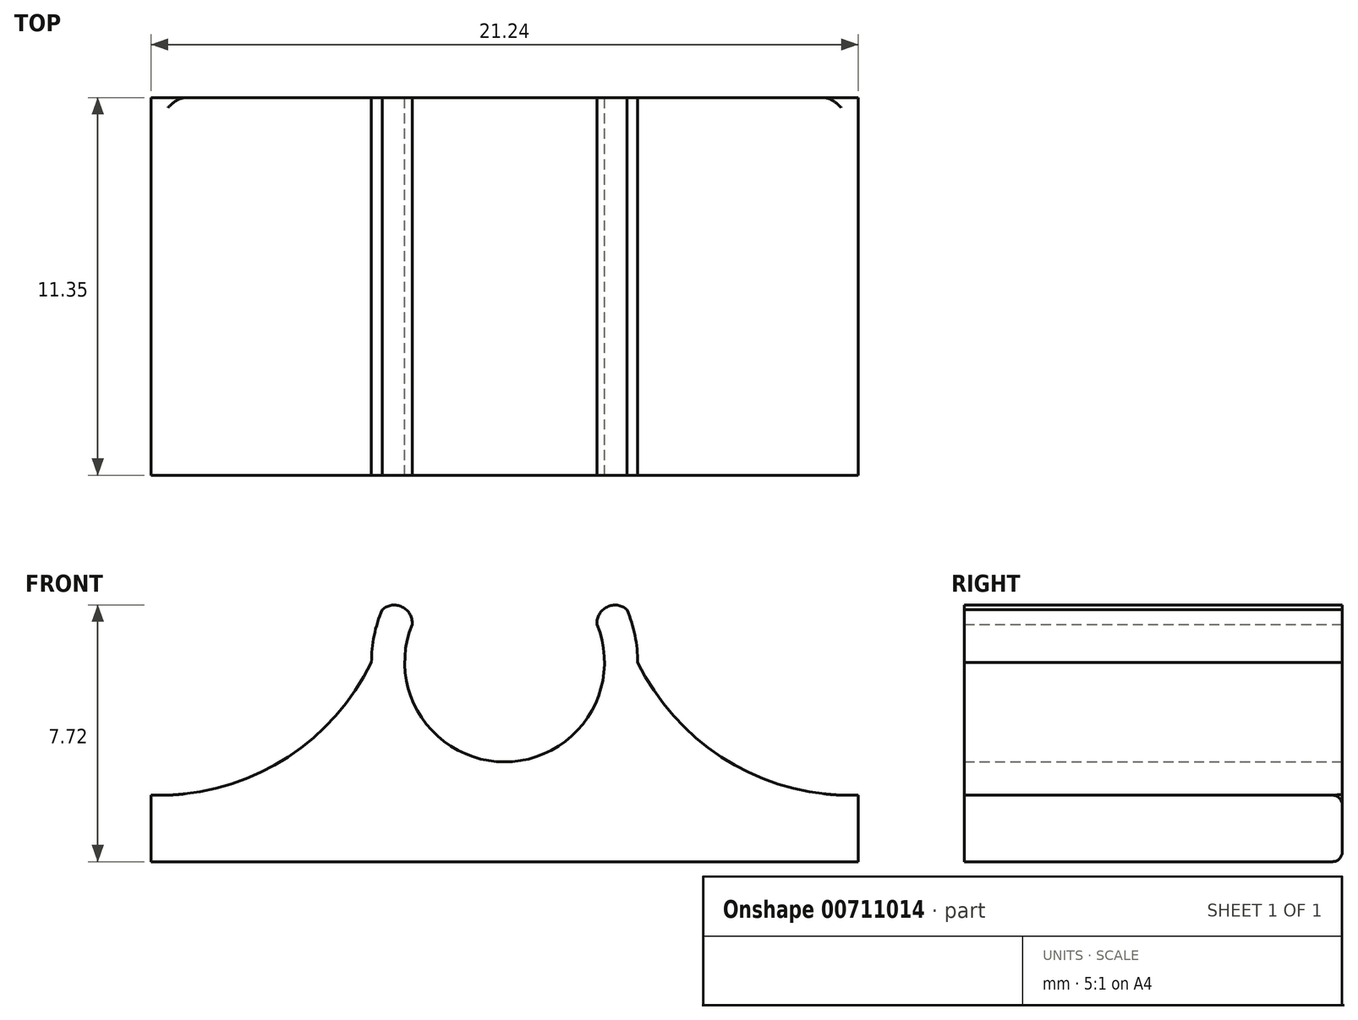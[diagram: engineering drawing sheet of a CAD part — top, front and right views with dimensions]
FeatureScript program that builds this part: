
annotation { "Feature Type Name" : "Feature", "Feature Type Description" : "" }
export const myFeature = defineFeature(function(context is Context, id is Id, definition is map)
    precondition{}
    {
        {
            var Q0;
            Q0=qCreatedBy(makeId("Top.planeOp"),FACE);
            var sketch = newSketch(context, id + "F0", { "sketchPlane" : qUnion([Q0])});
            skLineSegment(sketch, "E0.bottom", {"start": v(-45, 20) * mm, "end": v(45, 20) * mm});
            skLineSegment(sketch, "E0.top", {"start": v(-45, -20) * mm, "end": v(45, -20) * mm});
            skLineSegment(sketch, "E0.left", {"start": v(-55, 10) * mm, "end": v(-55, -10) * mm});
            skLineSegment(sketch, "E0.right", {"start": v(55, 10) * mm, "end": v(55, -10) * mm});
            skPoint(sketch, "E1.visualSharp", {"position": v(-55, 20) * mm});
            skArc(sketch, "E1.filletArc", {"start": v(-45, 20) * mm, "mid": v(-52.07, 17.07) * mm, "end": v(-55, 10) * mm});
            skPoint(sketch, "E2.visualSharp", {"position": v(55, 20) * mm});
            skArc(sketch, "E2.filletArc", {"start": v(55, 10) * mm, "mid": v(52.07, 17.07) * mm, "end": v(45, 20) * mm});
            skPoint(sketch, "E3.visualSharp", {"position": v(55, -20) * mm});
            skArc(sketch, "E3.filletArc", {"start": v(45, -20) * mm, "mid": v(52.07, -17.07) * mm, "end": v(55, -10) * mm});
            skPoint(sketch, "E4.visualSharp", {"position": v(-55, -20) * mm});
            skArc(sketch, "E4.filletArc", {"start": v(-55, -10) * mm, "mid": v(-52.07, -17.07) * mm, "end": v(-45, -20) * mm});
            skSolve(sketch);
        }
        {
            var Q0;
            Q0=qSketchRegion(id+"F0",true);
            extrude(context, id + "F1", {"entities" : qUnion([Q0]), "depth" : 2 * mm, "offsetDistance" : 25 * mm});
        }
        {
            var Q0;
            Q0=makeQuery(id+"F1.opExtrude","SWEPT_FACE",FACE,{"disambiguationData":[OSD([sQuery(id+"F0.wireOp",EDGE,"E0.bottom")])]});
            var sketch = newSketch(context, id + "F2", { "sketchPlane" : qUnion([Q0])});
            skArc(sketch, "E5", {"start": v(-2.78, 7.13) * mm, "mid": v(0, 3) * mm, "end": v(2.78, 7.13) * mm});
            skArc(sketch, "E6", {"start": v(-3.67, 7.58) * mm, "mid": v(-3.92, 6.8) * mm, "end": v(-4, 6) * mm});
            skArc(sketch, "E7", {"start": v(4, 6) * mm, "mid": v(6.5, 3.15) * mm, "end": v(10.12, 2) * mm});
            skArc(sketch, "E8.MirrorCS", {"start": v(-4, 6) * mm, "mid": v(-6.5, 3.15) * mm, "end": v(-10.12, 2) * mm});
            skArc(sketch, "E9", {"start": v(3.67, 7.58) * mm, "mid": v(3.08, 7.66) * mm, "end": v(2.78, 7.13) * mm});
            skArc(sketch, "E10.MirrorCS", {"start": v(-3.67, 7.58) * mm, "mid": v(-3.08, 7.66) * mm, "end": v(-2.78, 7.13) * mm});
            skArc(sketch, "E11.trimOffspring", {"start": v(4, 6) * mm, "mid": v(3.92, 6.8) * mm, "end": v(3.67, 7.58) * mm});
            skLineSegment(sketch, "E12", {"start": v(-10.12, 2) * mm, "end": v(10.12, 2) * mm});
            skSolve(sketch);
        }
        {
            var Q0;
            Q0=qSketchRegion(id+"F2",true);
            var Q1;
            Q1=makeQuery(id+"F1.opExtrude","SWEPT_FACE",FACE,{"disambiguationData":[OSD([sQuery(id+"F0.wireOp",EDGE,"E0.top")])]});
            extrude(context, id + "F3", {"entities" : qUnion([Q0]), "operationType" : NewBodyOperationType.ADD, "endBound" : BoundingType.UP_TO_SURFACE, "oppositeDirection" : true, "depth" : 25 * mm, "endBoundEntityFace" : qUnion([Q1]), "offsetDistance" : 25 * mm});
        }
        {
            var Q0;
            Q0=makeQuery(id+"F1.opExtrude","CAP_FACE",FACE,{"disambiguationData":[OSD([sQuery(id+"F0.wireOp",EDGE,"E0.bottom"),sQuery(id+"F0.wireOp",EDGE,"E0.top"),sQuery(id+"F0.wireOp",EDGE,"E0.left"),sQuery(id+"F0.wireOp",EDGE,"E0.right"),sQuery(id+"F0.wireOp",EDGE,"E1.filletArc"),sQuery(id+"F0.wireOp",EDGE,"E2.filletArc"),sQuery(id+"F0.wireOp",EDGE,"E3.filletArc"),sQuery(id+"F0.wireOp",EDGE,"E4.filletArc")])],"isStart":true});
            var Q1;
            {var subQ0=sQuery(id+"F0.wireOp",EDGE,"E2.filletArc");var subQ1=sQuery(id+"F0.wireOp",EDGE,"E0.top");var subQ3=sQuery(id+"F0.wireOp",EDGE,"E0.right");var subQ4=sQuery(id+"F0.wireOp",EDGE,"E0.bottom");var subQ5=sQuery(id+"F0.wireOp",EDGE,"E3.filletArc");Q1=makeQuery(id+"F3.boolean.opBoolean","SPLIT",FACE,{"disambiguationData":[TD([makeQuery(id+"F1.opExtrude","SWEPT_FACE",FACE,{"disambiguationData":[OSD([subQ3])]})])],"derivedFrom":makeQuery(id+"F1.opExtrude","CAP_FACE",FACE,{"disambiguationData":[OSD([subQ4,subQ1,sQuery(id+"F0.wireOp",EDGE,"E0.left"),subQ3,sQuery(id+"F0.wireOp",EDGE,"E1.filletArc"),subQ0,subQ5,sQuery(id+"F0.wireOp",EDGE,"E4.filletArc")])],"isStart":false})});}
            var Q2;
            {var subQ0=sQuery(id+"F0.wireOp",EDGE,"E1.filletArc");var subQ1=sQuery(id+"F0.wireOp",EDGE,"E0.left");var subQ2=sQuery(id+"F0.wireOp",EDGE,"E0.top");var subQ4=sQuery(id+"F0.wireOp",EDGE,"E0.bottom");var subQ5=sQuery(id+"F0.wireOp",EDGE,"E4.filletArc");Q2=makeQuery(id+"F3.boolean.opBoolean","SPLIT",FACE,{"disambiguationData":[TD([makeQuery(id+"F1.opExtrude","SWEPT_FACE",FACE,{"disambiguationData":[OSD([subQ1])]})])],"derivedFrom":makeQuery(id+"F1.opExtrude","CAP_FACE",FACE,{"disambiguationData":[OSD([subQ4,subQ2,subQ1,sQuery(id+"F0.wireOp",EDGE,"E0.right"),subQ0,sQuery(id+"F0.wireOp",EDGE,"E2.filletArc"),sQuery(id+"F0.wireOp",EDGE,"E3.filletArc"),subQ5])],"isStart":false})});}
            fillet(context, id + "F4", {"entities" : qUnion([Q0, Q1, Q2]), "radius" : .3 * mm, "tangentPropagation" : true, "allowEdgeOverflow" : false});
        }
        {
            var Q0;
            {var subQ0=sQuery(id+"F0.wireOp",EDGE,"E1.filletArc");var subQ1=sQuery(id+"F0.wireOp",EDGE,"E0.left");var subQ2=sQuery(id+"F0.wireOp",EDGE,"E0.top");var subQ4=sQuery(id+"F0.wireOp",EDGE,"E0.bottom");var subQ5=sQuery(id+"F0.wireOp",EDGE,"E4.filletArc");Q0=makeQuery(id+"F3.boolean.opBoolean","SPLIT",FACE,{"disambiguationData":[TD([makeQuery(id+"F1.opExtrude","SWEPT_FACE",FACE,{"disambiguationData":[OSD([subQ1])]})])],"derivedFrom":makeQuery(id+"F1.opExtrude","CAP_FACE",FACE,{"disambiguationData":[OSD([subQ4,subQ2,subQ1,sQuery(id+"F0.wireOp",EDGE,"E0.right"),subQ0,sQuery(id+"F0.wireOp",EDGE,"E2.filletArc"),sQuery(id+"F0.wireOp",EDGE,"E3.filletArc"),subQ5])],"isStart":false})});}
            var sketch = newSketch(context, id + "F5", { "sketchPlane" : qUnion([Q0])});
            skLineSegment(sketch, "E13.bottom", {"start": v(-58.42, 6.73) * mm, "end": v(65.85, 6.73) * mm});
            skLineSegment(sketch, "E13.top", {"start": v(-58.42, -28.13) * mm, "end": v(65.85, -28.13) * mm});
            skLineSegment(sketch, "E13.left", {"start": v(-58.42, 6.73) * mm, "end": v(-58.42, -28.13) * mm});
            skLineSegment(sketch, "E13.right", {"start": v(65.85, 6.73) * mm, "end": v(65.85, -28.13) * mm});
            skLineSegment(sketch, "E14.bottom", {"start": v(-10.62, 21.12) * mm, "end": v(-58.42, 21.12) * mm});
            skLineSegment(sketch, "E14.top", {"start": v(-10.62, 6.73) * mm, "end": v(-58.42, 6.73) * mm});
            skLineSegment(sketch, "E14.left", {"start": v(-10.62, 21.12) * mm, "end": v(-10.62, 6.73) * mm});
            skLineSegment(sketch, "E14.right", {"start": v(-58.42, 21.12) * mm, "end": v(-58.42, 6.73) * mm});
            skLineSegment(sketch, "E15.MirrorCS", {"start": v(10.62, 21.12) * mm, "end": v(58.42, 21.12) * mm});
            skLineSegment(sketch, "E16.MirrorCS", {"start": v(58.42, 21.12) * mm, "end": v(58.42, 6.73) * mm});
            skLineSegment(sketch, "E17.MirrorCS", {"start": v(10.62, 21.12) * mm, "end": v(10.62, 6.73) * mm});
            skLineSegment(sketch, "E18.MirrorCS", {"start": v(58.42, 6.73) * mm, "end": v(-65.85, 6.73) * mm});
            skSolve(sketch);
        }
        {
            var Q0;
            Q0 = qSketchRegion(id + "F5", true);
            extrude(context, id + "F6", {"entities" : qUnion([Q0]), "operationType" : NewBodyOperationType.REMOVE, "oppositeDirection" : true, "depth" : 25 * mm, "offsetDistance" : 25 * mm});
        }
        {
            var Q0;
            Q0=qCreatedBy(makeId("Top.planeOp"),FACE);
            var sketch = newSketch(context, id + "F7", { "sketchPlane" : qUnion([Q0])});
            skLineSegment(sketch, "E19.bottom", {"start": v(-31.93, 8.65) * mm, "end": v(20.15, 8.65) * mm});
            skLineSegment(sketch, "E19.top", {"start": v(-31.93, -22.67) * mm, "end": v(20.15, -22.67) * mm});
            skLineSegment(sketch, "E19.left", {"start": v(-31.93, 8.65) * mm, "end": v(-31.93, -22.67) * mm});
            skLineSegment(sketch, "E19.right", {"start": v(20.15, 8.65) * mm, "end": v(20.15, -22.67) * mm});
            skSolve(sketch);
        }
        {
            var Q0;
            Q0 = qSketchRegion(id + "F7", true);
            extrude(context, id + "F8", {"entities" : qUnion([Q0]), "operationType" : NewBodyOperationType.REMOVE, "depth" : 25 * mm, "offsetDistance" : 25 * mm});
        }
    });
